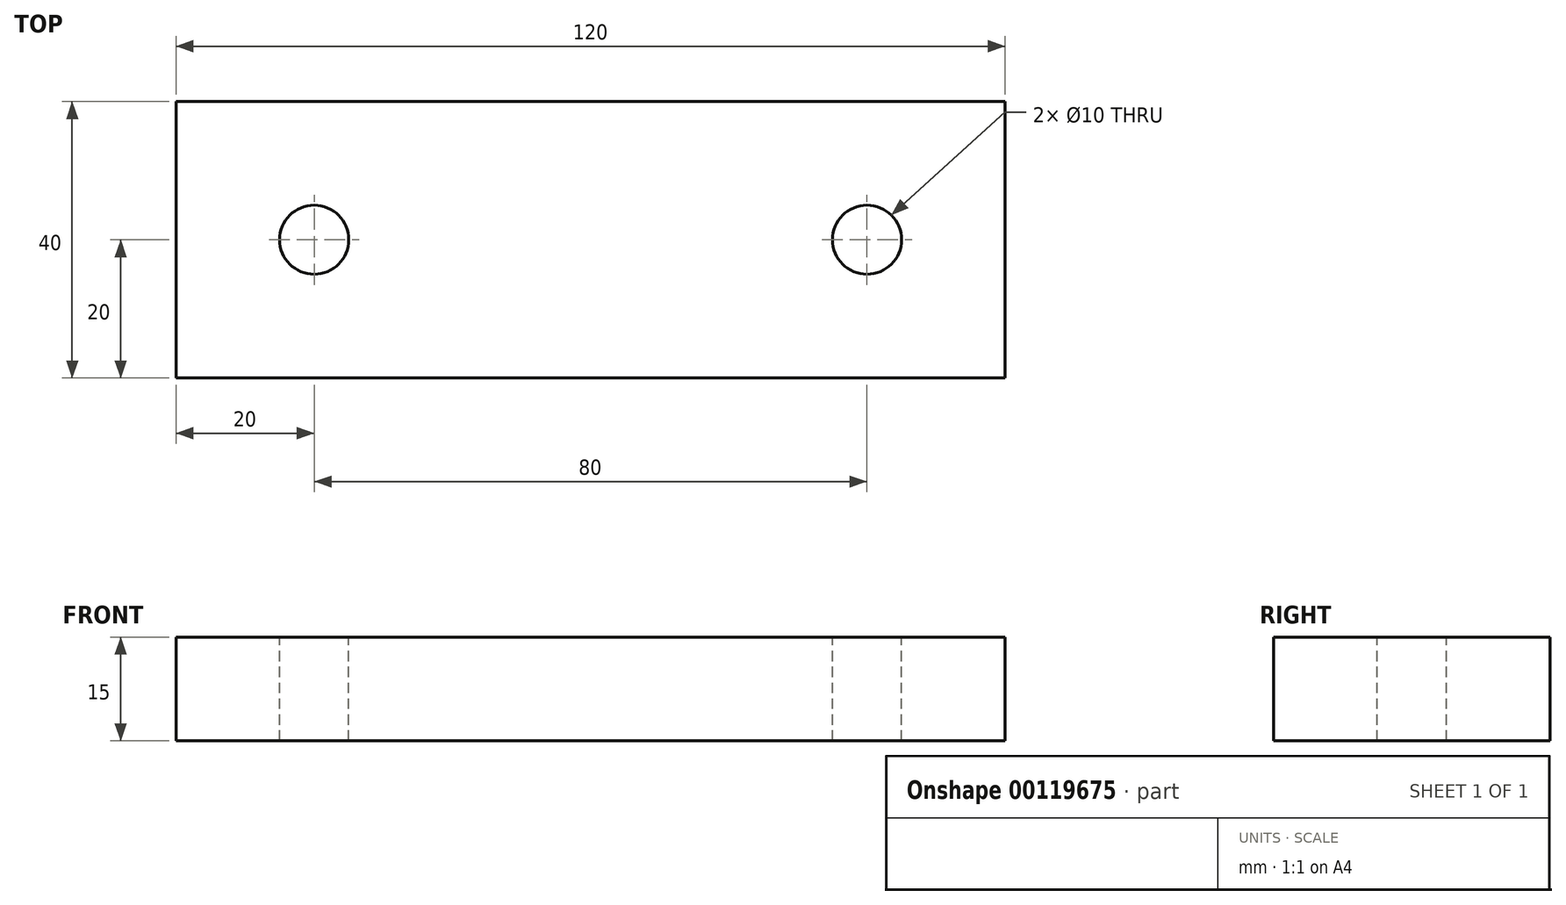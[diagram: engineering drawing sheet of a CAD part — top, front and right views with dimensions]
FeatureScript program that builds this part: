
annotation { "Feature Type Name" : "Feature", "Feature Type Description" : "" }
export const myFeature = defineFeature(function(context is Context, id is Id, definition is map)
    precondition{}
    {
        {
            var Q0;
            Q0=qCreatedBy(makeId("Front.planeOp"),FACE);
            var sketch = newSketch(context, id + "F0", { "sketchPlane" : qUnion([Q0])});
            skLineSegment(sketch, "E0.bottom", {"start": v(0, 0) * mm, "end": v(120, 0) * mm});
            skLineSegment(sketch, "E0.top", {"start": v(0, -15) * mm, "end": v(120, -15) * mm});
            skLineSegment(sketch, "E0.left", {"start": v(0, 0) * mm, "end": v(0, -15) * mm});
            skLineSegment(sketch, "E0.right", {"start": v(120, 0) * mm, "end": v(120, -15) * mm});
            skSolve(sketch);
        }
        {
            var Q0;
            Q0=makeQuery(id+"F0.imprint","IMPRINT",FACE,{"disambiguationData":[TD([[makeQuery(id+"F0.imprint","IMPRINT",EDGE,{"derivedFrom":sQuery(id+"F0.wireOp",EDGE,"E0.bottom")}),-1.0]])]});
            extrude(context, id + "F1", {"entities" : qUnion([Q0]), "endBound" : BoundingType.SYMMETRIC, "depth" : 40 * mm});
        }
        {
            var Q0;
            Q0=makeQuery(id+"F1.opExtrude","SWEPT_FACE",FACE,{"disambiguationData":[OSD([sQuery(id+"F0.wireOp",EDGE,"E0.bottom")])]});
            var sketch = newSketch(context, id + "F2", { "sketchPlane" : qUnion([Q0])});
            skCircle(sketch, "E1", {"center": v(20, 0) * mm, "radius": 5 * mm});
            skCircle(sketch, "E2", {"center": v(100, 0) * mm, "radius": 5 * mm});
            skSolve(sketch);
        }
        {
            var Q0;
            Q0=makeQuery(id+"F2.imprint","IMPRINT",FACE,{"disambiguationData":[TD([[makeQuery(id+"F2.imprint","IMPRINT",EDGE,{"derivedFrom":sQuery(id+"F2.wireOp",EDGE,"E1")}),1.0]])]});
            var Q1;
            Q1=makeQuery(id+"F2.imprint","IMPRINT",FACE,{"disambiguationData":[TD([[makeQuery(id+"F2.imprint","IMPRINT",EDGE,{"derivedFrom":sQuery(id+"F2.wireOp",EDGE,"E2")}),1.0]])]});
            extrude(context, id + "F3", {"entities" : qUnion([Q0, Q1]), "operationType" : NewBodyOperationType.REMOVE, "endBound" : BoundingType.THROUGH_ALL, "oppositeDirection" : true, "depth" : 25 * mm});
        }
    });
